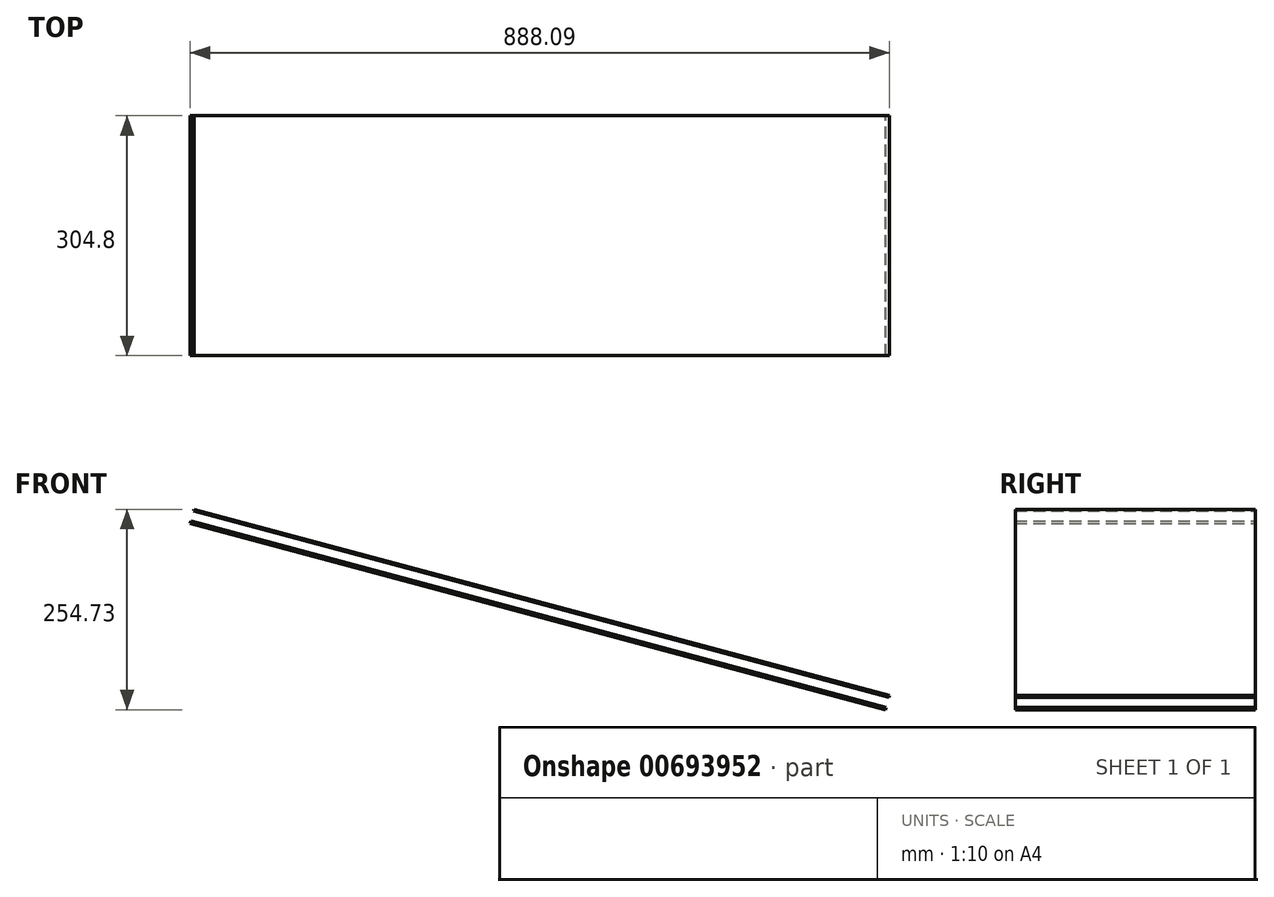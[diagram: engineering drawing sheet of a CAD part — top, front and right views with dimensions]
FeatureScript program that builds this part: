
annotation { "Feature Type Name" : "Feature", "Feature Type Description" : "" }
export const myFeature = defineFeature(function(context is Context, id is Id, definition is map)
    precondition{}
    {
        {
            var Q0;
            Q0=qCreatedBy(makeId("Front.planeOp"),FACE);
            var sketch = newSketch(context, id + "F0", { "sketchPlane" : qUnion([Q0])});
            skLineSegment(sketch, "E0", {"start": v(-441.62, 118.33) * mm, "end": v(-441, 120.63) * mm});
            skLineSegment(sketch, "E1", {"start": v(-441, 120.63) * mm, "end": v(442.24, -116.03) * mm});
            skLineSegment(sketch, "E2", {"start": v(442.24, -116.03) * mm, "end": v(441.62, -118.33) * mm});
            skLineSegment(sketch, "E3", {"start": v(441.62, -118.33) * mm, "end": v(-441.62, 118.33) * mm});
            skSolve(sketch);
        }
        {
            var Q0;
            Q0=makeQuery(id+"F0.imprint","IMPRINT",FACE,{"disambiguationData":[TD([[makeQuery(id+"F0.imprint","IMPRINT",EDGE,{"derivedFrom":sQuery(id+"F0.wireOp",EDGE,"E0")}),-1.0]])]});
            extrude(context, id + "F1", {"entities" : qUnion([Q0]), "endBound" : BoundingType.SYMMETRIC, "depth" : 304.8 * mm, "offsetDistance" : 25.4 * mm});
        }
        {
            var Q0;
            Q0=qCreatedBy(makeId("Front.planeOp"),FACE);
            var sketch = newSketch(context, id + "F2", { "sketchPlane" : qUnion([Q0])});
            skLineSegment(sketch, "E4", {"start": v(-445.85, 102.57) * mm, "end": v(-445.02, 105.63) * mm});
            skLineSegment(sketch, "E5", {"start": v(-445.02, 105.63) * mm, "end": v(438.22, -131.03) * mm});
            skLineSegment(sketch, "E6", {"start": v(438.22, -131.03) * mm, "end": v(437.4, -134.1) * mm});
            skLineSegment(sketch, "E7", {"start": v(437.4, -134.1) * mm, "end": v(-445.85, 102.57) * mm});
            skPoint(sketch, "E8", {"position": v(-441, 120.63) * mm});
            skLineSegment(sketch, "E9", {"start": v(-445.85, 102.57) * mm, "end": v(-441, 120.63) * mm, "construction": true});
            skLineSegment(sketch, "E10", {"start": v(442.24, -116.03) * mm, "end": v(437.4, -134.1) * mm, "construction": true});
            skLineSegment(sketch, "E11", {"start": v(-445.02, 105.63) * mm, "end": v(-394.22, 105.63) * mm, "construction": true});
            skSolve(sketch);
        }
        {
            var Q0;
            Q0=makeQuery(id+"F2.imprint","IMPRINT",FACE,{"disambiguationData":[TD([[makeQuery(id+"F2.imprint","IMPRINT",EDGE,{"derivedFrom":sQuery(id+"F2.wireOp",EDGE,"E4")}),-1.0]])]});
            extrude(context, id + "F3", {"entities" : qUnion([Q0]), "endBound" : BoundingType.SYMMETRIC, "depth" : 304.8 * mm, "offsetDistance" : 25.4 * mm});
        }
    });
